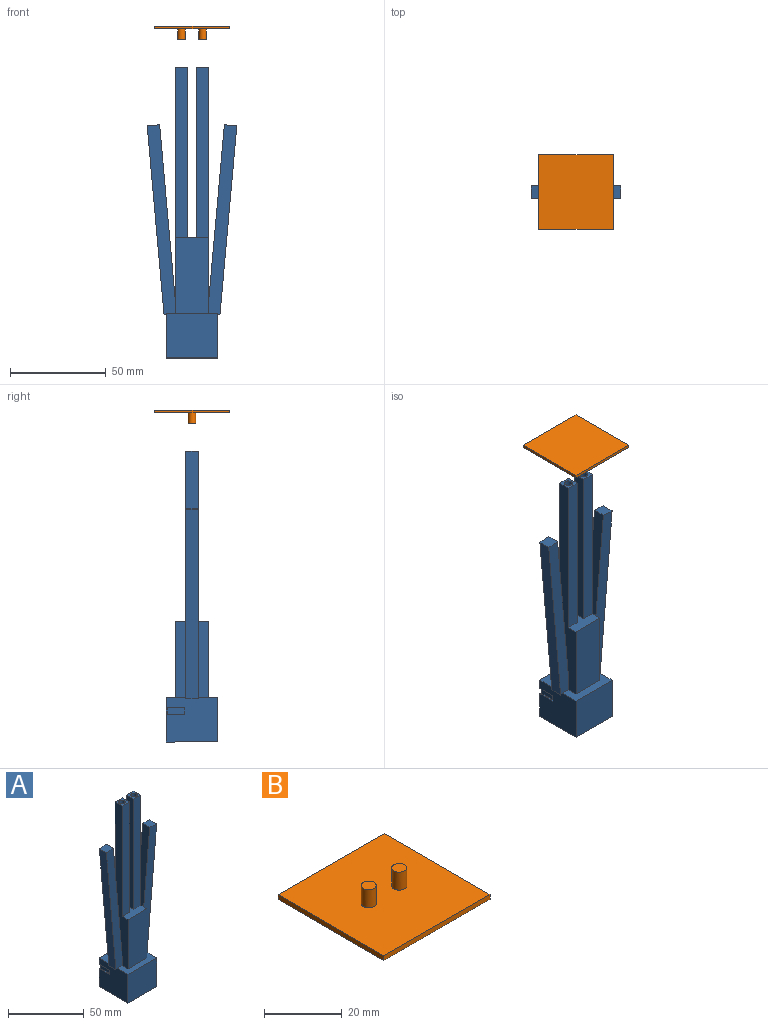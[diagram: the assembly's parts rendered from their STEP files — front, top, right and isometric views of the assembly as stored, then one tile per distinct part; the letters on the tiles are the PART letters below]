
ASSEMBLY  parts=2 mates=1
PART A: 146 faces, bbox 46.8x26.7x151.8 mm
  f0: plane 39.7x17.69mm, normal (0,1,0), area 588.8mm2, adj f9,f15,f16,f32,f48,f49,f50,f51
  f1: plane 26.69x23.07mm, normal (0,1,0), area 551.4mm2, adj f2,f3,f4,f5,f12,f21,f32,f43
  f2: plane 26.69x23.07mm, normal (-1,0,0), area 580.5mm2, adj f1,f17,f18,f21,f22,f25,f31,f32
  f3: plane 3.38x0.75mm, normal (1,0,0), area 2.5mm2, adj f1,f4,f5,f41
  f4: plane 9.49x9.49mm, normal (0,0,-1), area 13.7mm2, adj f1,f3,f12,f39,f40,f41
  f5: plane 9.49x9.49mm, normal (0,0,1), area 13.7mm2, adj f1,f3,f12,f39,f40,f41
  f6: plane 90.28x8.06mm, normal (-1,0,0.09), area 592.6mm2, adj f16,f19,f20,f28
  f7: plane 90.28x8.06mm, normal (1,0,0.09), area 592.6mm2, adj f15,f17,f18,f23
  f8: plane 39.7x17.69mm, normal (0,-1,0), area 702.1mm2, adj f9,f15,f16,f31
  f9: plane 17.69x17.69mm, normal (0,0,1), area 227.3mm2, adj f0,f8,f13,f14,f15,f16,f29,f30
  f10: plane 6.54x6.54mm, normal (0,0,1), area 29.9mm2, adj f14,f15,f30,f34,f38
  f11: plane 6.54x6.54mm, normal (0,0,1), area 29.9mm2, adj f13,f16,f29,f33,f36
  f12: plane 26.69x23.07mm, normal (1,0,0), area 580.5mm2, adj f1,f4,f5,f19,f20,f21,f22,f26
  f13: plane 89.02x6.54mm, normal (-1,0,0), area 582mm2, adj f9,f11,f29,f33
  f14: plane 89.02x6.54mm, normal (1,0,0), area 582mm2, adj f9,f10,f30,f34
  f15: plane 128.71x17.69mm, normal (-1,0,0), area 1229.2mm2, adj f0,f7,f8,f9,f10,f17,f18,f30
  f16: plane 128.71x17.69mm, normal (1,0,0), area 1229.2mm2, adj f0,f6,f8,f9,f11,f19,f20,f29
  f17: plane 99.26x14.57mm, normal (0,-1,0), area 643.4mm2, adj f2,f7,f15,f23,f24,f25,f31
  f18: plane 99.26x14.57mm, normal (0,1,0), area 643.4mm2, adj f2,f7,f15,f23,f24,f25,f32
  f19: plane 99.26x14.57mm, normal (0,1,0), area 643.4mm2, adj f6,f12,f16,f26,f27,f28,f32
  f20: plane 99.26x14.57mm, normal (0,-1,0), area 643.4mm2, adj f6,f12,f16,f26,f27,f28,f31
  f21: plane 26.69x26.69mm, normal (0,0,-1), area 712.2mm2, adj f1,f2,f12,f22
  f22: plane 26.69x23.07mm, normal (0,-1,0), area 615.6mm2, adj f2,f12,f21,f31
  f23: plane 6.54x6.51mm, normal (-0.09,0,1), area 42.7mm2, adj f7,f17,f18,f24
  f24: plane 98.68x8.81mm, normal (-1,0,-0.09), area 647.7mm2, adj f17,f18,f23,f25
  f25: plane 6.54x1.26mm, normal (0.09,0,-1), area 8.3mm2, adj f2,f17,f18,f24
  f26: plane 6.54x1.26mm, normal (-0.09,0,-1), area 8.3mm2, adj f12,f19,f20,f27
  f27: plane 98.68x8.81mm, normal (1,0,-0.09), area 647.7mm2, adj f19,f20,f26,f28
  f28: plane 6.54x6.51mm, normal (0.09,0,1), area 42.7mm2, adj f6,f19,f20,f27
  f29: plane 89.02x6.54mm, normal (0,-1,0), area 582mm2, adj f9,f11,f13,f16
  f30: plane 89.02x6.54mm, normal (0,-1,0), area 582mm2, adj f9,f10,f14,f15
  f31: plane 26.69x10.07mm, normal (0,0,1), area 170.3mm2, adj f2,f8,f12,f15,f16,f17,f20,f22
  f32: plane 26.69x10.07mm, normal (0,0,1), area 170.3mm2, adj f0,f1,f2,f12,f15,f16,f18,f19
  f33: plane 89.02x6.54mm, normal (0,1,0), area 582mm2, adj f9,f11,f13,f16
  f34: plane 89.02x6.54mm, normal (0,1,0), area 582mm2, adj f9,f10,f14,f15
  f35: plane 4.05x4.05mm, normal (0,0,1), area 12.9mm2, adj f36
  f36: cylinder r=2.02mm len=6mm, axis (0,0,1), area 76.3mm2, adj f11,f35
  f37: plane 4.05x4.05mm, normal (0,0,1), area 12.9mm2, adj f38
  f38: cylinder r=2.02mm len=6mm, axis (0,0,1), area 76.3mm2, adj f10,f37
  f39: plane 3.38x0.75mm, normal (0,1,0), area 2.5mm2, adj f4,f5,f12,f40
  f40: plane 8.74x3.38mm, normal (1,0,0), area 29.6mm2, adj f4,f5,f39,f41
  f41: plane 8.74x3.38mm, normal (0,1,0), area 29.6mm2, adj f3,f4,f5,f40
  f42: plane 8.74x3.38mm, normal (-1,0,0), area 29.6mm2, adj f43,f44,f45,f46
  f43: plane 9.49x9.49mm, normal (0,0,-1), area 13.7mm2, adj f1,f2,f42,f45,f46,f47
  f44: plane 9.49x9.49mm, normal (0,0,1), area 13.7mm2, adj f1,f2,f42,f45,f46,f47
  f45: plane 3.38x0.75mm, normal (0,1,0), area 2.5mm2, adj f2,f42,f43,f44
  f46: plane 8.74x3.38mm, normal (0,1,0), area 29.6mm2, adj f42,f43,f44,f47
  f47: plane 3.38x0.75mm, normal (-1,0,0), area 2.5mm2, adj f1,f43,f44,f46
  f48: plane 3.04x3mm, normal (0,0,1), area 9.1mm2, adj f0,f49,f69,f70
  f49: plane 3x0.89mm, normal (-1,0,0), area 2.7mm2, adj f0,f48,f50,f70
  f50: plane 3x0.79mm, normal (-0.19,0,-0.98), area 2.4mm2, adj f0,f49,f51,f70
  f51: plane 6.3x3mm, normal (-1,0,0), area 18.9mm2, adj f0,f50,f52,f70
  f52: plane 3x1.47mm, normal (0,0,-1), area 4.4mm2, adj f0,f51,f53,f70
  f53: plane 4.94x3mm, normal (0.86,0,-0.51), area 17.3mm2, adj f0,f52,f54,f70
  f54: plane 3x0.03mm, normal (-0.21,0,-0.98), area 0.1mm2, adj f0,f53,f55,f70
  f55: plane 3.9x3mm, normal (-1,0,0), area 11.7mm2, adj f0,f54,f56,f70
  f56: plane 3x0.79mm, normal (-0.19,0,0.98), area 2.4mm2, adj f0,f55,f57,f70
  f57: plane 3x0.88mm, normal (-1,0,0), area 2.6mm2, adj f0,f56,f58,f70
  f58: plane 3.04x3mm, normal (0,0,-1), area 9.1mm2, adj f0,f57,f59,f70
  f59: plane 3x0.88mm, normal (1,0,0), area 2.6mm2, adj f0,f58,f60,f70
  f60: plane 3x0.78mm, normal (0.19,0,0.98), area 2.4mm2, adj f0,f59,f61,f70
  f61: plane 5.27x3mm, normal (1,0,0), area 15.8mm2, adj f0,f60,f62,f70
  f62: plane 3x0.78mm, normal (0.19,0,-0.98), area 2.4mm2, adj f0,f61,f63,f70
  f63: plane 3x0.89mm, normal (1,0,0), area 2.7mm2, adj f0,f62,f64,f70
  f64: plane 3x2.25mm, normal (0,0,1), area 6.8mm2, adj f0,f63,f65,f70
  f65: plane 4.94x3mm, normal (-0.86,0,0.51), area 17.3mm2, adj f0,f64,f66,f70
  f66: plane 3x0.03mm, normal (0.16,0,0.99), area 0.1mm2, adj f0,f65,f67,f70
  f67: plane 3.9x3mm, normal (1,0,0), area 11.7mm2, adj f0,f66,f68,f70
  f68: plane 3x0.79mm, normal (0.19,0,-0.98), area 2.4mm2, adj f0,f67,f69,f70
  f69: plane 3x0.89mm, normal (1,0,0), area 2.7mm2, adj f0,f48,f68,f70
  f70: plane 7.5x7.34mm, normal (0,1,0), area 32.4mm2, adj f48,f49,f50,f51,f52,f53,f54,f55
  f71: plane 3x0.67mm, normal (1,0,0), area 2mm2, adj f0,f72,f90,f91
  f72: plane 3x0.58mm, normal (0.14,0,0.99), area 1.7mm2, adj f0,f71,f73,f91
  f73: plane 7.03x3mm, normal (0.93,0,0.36), area 22.6mm2, adj f0,f72,f74,f91
  f74: plane 3x0.9mm, normal (0,0,1), area 2.7mm2, adj f0,f73,f75,f91
  f75: plane 7.03x3mm, normal (-0.93,0,0.36), area 22.6mm2, adj f0,f74,f76,f91
  f76: plane 3x0.57mm, normal (-0.14,0,0.99), area 1.7mm2, adj f0,f75,f77,f91
  f77: plane 3x0.67mm, normal (-1,0,0), area 2mm2, adj f0,f76,f78,f91
  f78: plane 3x2.23mm, normal (0,0,-1), area 6.7mm2, adj f0,f77,f79,f91
  f79: plane 3x0.67mm, normal (1,0,0), area 2mm2, adj f0,f78,f80,f91
  f80: plane 3x0.59mm, normal (0.17,0,0.99), area 1.8mm2, adj f0,f79,f81,f91
  f81: plane 3x1.43mm, normal (0.94,0,-0.34), area 4.6mm2, adj f0,f80,f82,f91
  f82: plane 3.12x3mm, normal (0,0,-1), area 9.3mm2, adj f0,f81,f83,f91
  f83: plane 3x1.43mm, normal (-0.94,0,-0.35), area 4.6mm2, adj f0,f82,f84,f91
  f84: plane 3x0.59mm, normal (-0.17,0,0.99), area 1.8mm2, adj f0,f83,f85,f91
  f85: plane 3x0.67mm, normal (-1,0,0), area 2mm2, adj f0,f84,f90,f91
  f86: plane 3.34x3mm, normal (-0.94,0,-0.35), area 10.7mm2, adj f87,f89,f91,f92
  f87: plane 3x2.47mm, normal (0,0,1), area 7.4mm2, adj f86,f88,f91,f92
  f88: plane 3.34x3mm, normal (0.94,0,-0.34), area 10.7mm2, adj f87,f89,f91,f92
  f89: plane 3x0.03mm, normal (0,0,-1), area 0.1mm2, adj f86,f88,f91,f92
  f90: plane 3x2.23mm, normal (0,0,-1), area 6.7mm2, adj f0,f71,f85,f91
  f91: plane 7.78x7.44mm, normal (0,1,0), area 19.1mm2, adj f71,f72,f73,f74,f75,f76,f77,f78
  f92: plane 3.34x2.47mm, normal (0,1,0), area 4.2mm2, adj f86,f87,f88,f89
  f93: plane 3x0.95mm, normal (1,0,0), area 2.8mm2, adj f0,f94,f112,f113
  f94: plane 3x0.56mm, normal (0.14,0,0.99), area 1.7mm2, adj f0,f93,f95,f113
  f95: plane 6.85x3mm, normal (0.94,0,0.33), area 21.8mm2, adj f0,f94,f96,f113
  f96: plane 3x1.62mm, normal (0,0,1), area 4.8mm2, adj f0,f95,f97,f113
  f97: plane 6.85x3mm, normal (-0.94,0,0.33), area 21.7mm2, adj f0,f96,f98,f113
  f98: plane 3x0.56mm, normal (-0.14,0,0.99), area 1.7mm2, adj f0,f97,f99,f113
  f99: plane 3x0.95mm, normal (-1,0,0), area 2.8mm2, adj f0,f98,f100,f113
  f100: plane 3x2.68mm, normal (0,0,-1), area 8mm2, adj f0,f99,f101,f113
  f101: plane 3x0.95mm, normal (1,0,0), area 2.8mm2, adj f0,f100,f102,f113
  f102: plane 3x0.55mm, normal (0.17,0,0.98), area 1.7mm2, adj f0,f101,f103,f113
  f103: plane 3x1.08mm, normal (0.95,0,-0.3), area 3.4mm2, adj f0,f102,f104,f113
  f104: plane 3x2.55mm, normal (0,0,-1), area 7.7mm2, adj f0,f103,f105,f113
  f105: plane 3x1.08mm, normal (-0.95,0,-0.3), area 3.4mm2, adj f0,f104,f106,f113
  f106: plane 3x0.55mm, normal (-0.18,0,0.98), area 1.7mm2, adj f0,f105,f107,f113
  f107: plane 3x0.95mm, normal (-1,0,0), area 2.8mm2, adj f0,f106,f112,f113
  f108: plane 3x2.77mm, normal (-0.95,0,-0.3), area 8.7mm2, adj f109,f111,f113,f114
  f109: plane 3x1.81mm, normal (0,0,1), area 5.4mm2, adj f108,f110,f113,f114
  f110: plane 3x2.77mm, normal (0.95,0,-0.3), area 8.7mm2, adj f109,f111,f113,f114
  f111: plane 3x0.03mm, normal (0,0,-1), area 0.1mm2, adj f108,f110,f113,f114
  f112: plane 3x2.68mm, normal (0,0,-1), area 8mm2, adj f0,f93,f107,f113
  f113: plane 7.87x7.52mm, normal (0,1,0), area 27.1mm2, adj f93,f94,f95,f96,f97,f98,f99,f100
  f114: plane 2.77x1.81mm, normal (0,1,0), area 2.5mm2, adj f108,f109,f110,f111
  f115: plane 3x1.79mm, normal (-1,0,0), area 5.4mm2, adj f0,f116,f144,f145
  f116: plane 3x0.98mm, normal (0,0,-1), area 2.9mm2, adj f0,f115,f117,f145
  f117: plane 3x1.37mm, normal (0.98,0,-0.18), area 4.2mm2, adj f0,f116,f118,f145
  f118: extruded ~3x0.79mm, area 2.7mm2, adj f0,f117,f119,f145
  f119: extruded ~3x1.15mm, area 3.5mm2, adj f0,f118,f120,f145
  f120: extruded ~3x1.59mm, area 5mm2, adj f0,f119,f121,f145
  f121: extruded ~3x1.14mm, area 4mm2, adj f0,f120,f122,f145
  f122: extruded ~3x1.04mm, area 3.7mm2, adj f0,f121,f123,f145
  f123: extruded ~3x1.82mm, area 5.9mm2, adj f0,f122,f124,f145
  f124: extruded ~3x2.3mm, area 7.7mm2, adj f0,f123,f125,f145
  f125: extruded ~3x1.81mm, area 6.1mm2, adj f0,f124,f126,f145
  f126: extruded ~3x1.86mm, area 6.5mm2, adj f0,f125,f127,f145
  f127: extruded ~3x2.47mm, area 7.9mm2, adj f0,f126,f128,f145
  f128: extruded ~3x1.97mm, area 6mm2, adj f0,f127,f129,f145
  f129: extruded ~3x1.4mm, area 5.1mm2, adj f0,f128,f130,f145
  f130: plane 3x1.79mm, normal (1,0,0), area 5.4mm2, adj f0,f129,f131,f145
  f131: plane 3x0.98mm, normal (0,0,1), area 2.9mm2, adj f0,f130,f132,f145
  f132: plane 3x1.38mm, normal (-0.98,0,0.18), area 4.2mm2, adj f0,f131,f133,f145
  f133: extruded ~3x0.9mm, area 3.1mm2, adj f0,f132,f134,f145
  f134: extruded ~3x1.24mm, area 3.8mm2, adj f0,f133,f135,f145
  f135: extruded ~3x1.55mm, area 4.9mm2, adj f0,f134,f136,f145
  f136: extruded ~3x1.13mm, area 3.9mm2, adj f0,f135,f137,f145
  f137: extruded ~3x1.1mm, area 3.7mm2, adj f0,f136,f138,f145
  f138: extruded ~3x1.75mm, area 5.7mm2, adj f0,f137,f139,f145
  f139: extruded ~3x2.38mm, area 7.9mm2, adj f0,f138,f140,f145
  f140: extruded ~3x1.77mm, area 6.1mm2, adj f0,f139,f141,f145
  f141: extruded ~3x1.87mm, area 6.6mm2, adj f0,f140,f142,f145
  f142: extruded ~3x2.48mm, area 7.9mm2, adj f0,f141,f143,f145
  f143: extruded ~3x1.83mm, area 5.6mm2, adj f0,f142,f144,f145
  f144: extruded ~3x1.33mm, area 4.7mm2, adj f0,f115,f143,f145
  f145: plane 9.87x6.78mm, normal (0,1,0), area 27.9mm2, adj f115,f116,f117,f118,f119,f120,f121,f122
PART B: 10 faces, bbox 38.7x38.7x7.2 mm
  f0: plane 38.69x1.5mm, normal (0,-1,0), area 58mm2, adj f2,f3,f4,f5
  f1: plane 38.69x1.5mm, normal (0,1,0), area 58mm2, adj f2,f3,f4,f5
  f2: plane 38.69x1.5mm, normal (-1,0,0), area 58mm2, adj f0,f1,f4,f5
  f3: plane 38.69x1.5mm, normal (1,0,0), area 58mm2, adj f0,f1,f4,f5
  f4: plane 38.69x38.69mm, normal (0,0,-1), area 1496.7mm2, adj f0,f1,f2,f3
  f5: plane 38.69x38.69mm, normal (0,0,1), area 1472.8mm2, adj f0,f1,f2,f3,f6,f7
  f6: cylinder r=1.95mm len=5.7mm, axis (0,0,1), area 69.8mm2, adj f5,f8
  f7: cylinder r=1.95mm len=5.7mm, axis (0,0,1), area 69.8mm2, adj f5,f9
  f8: plane 3.9x3.9mm, normal (0,0,1), area 11.9mm2, adj f6
  f9: plane 3.9x3.9mm, normal (0,0,1), area 11.9mm2, adj f7
PLACE A rot(axis=(0,0,-1),0deg) t=(-177.88,-3.05,-28.81)mm
PLACE B rot(axis=(1,0,0),180deg) t=(-177.88,17.57,114.05)mm
MATE slider A.f36 <-> B.f7  axis (0,0,1) through (-56,8.68,116.97)mm
